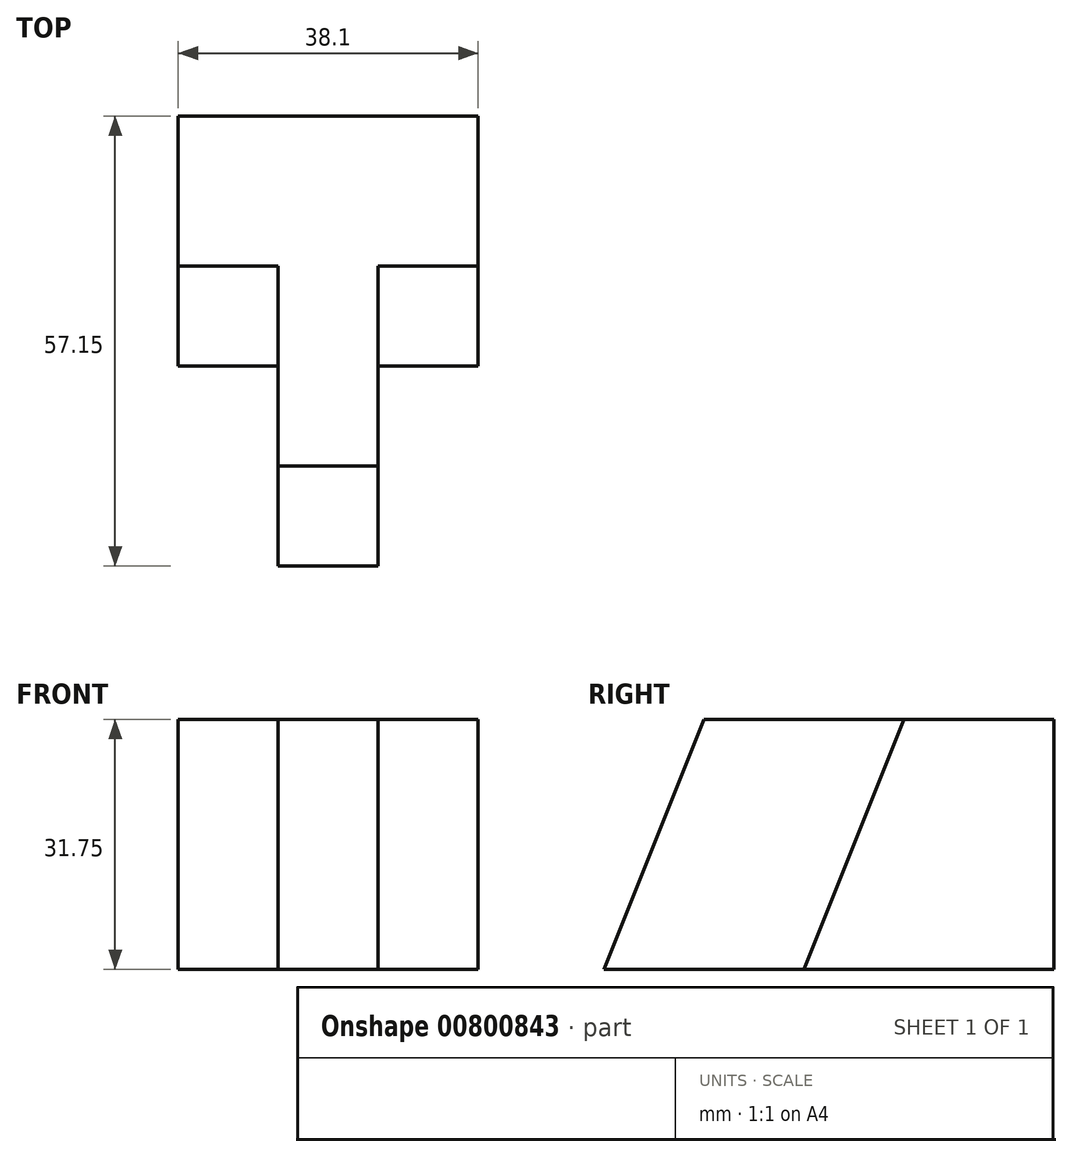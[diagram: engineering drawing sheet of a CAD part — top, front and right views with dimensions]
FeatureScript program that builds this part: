
annotation { "Feature Type Name" : "Feature", "Feature Type Description" : "" }
export const myFeature = defineFeature(function(context is Context, id is Id, definition is map)
    precondition{}
    {
        {
            var Q0;
            Q0=qCreatedBy(makeId("Top.planeOp"),FACE);
            var sketch = newSketch(context, id + "F0", { "sketchPlane" : qUnion([Q0])});
            skLineSegment(sketch, "E0", {"start": v(0, 0) * mm, "end": v(0, 57.15) * mm, "construction": true});
            skLineSegment(sketch, "E1", {"start": v(0, 57.15) * mm, "end": v(38.1, 57.15) * mm});
            skLineSegment(sketch, "E2", {"start": v(0, 57.15) * mm, "end": v(0, 25.4) * mm});
            skLineSegment(sketch, "E3", {"start": v(0, 25.4) * mm, "end": v(12.7, 25.4) * mm});
            skLineSegment(sketch, "E4", {"start": v(12.7, 25.4) * mm, "end": v(12.7, 0) * mm});
            skLineSegment(sketch, "E5", {"start": v(38.1, 57.15) * mm, "end": v(38.1, 25.4) * mm});
            skLineSegment(sketch, "E6", {"start": v(38.1, 25.4) * mm, "end": v(25.4, 25.4) * mm});
            skLineSegment(sketch, "E7", {"start": v(25.4, 25.4) * mm, "end": v(25.4, 0) * mm});
            skLineSegment(sketch, "E8", {"start": v(25.4, 0) * mm, "end": v(12.7, 0) * mm});
            skSolve(sketch);
        }
        {
            var Q0;
            Q0=makeQuery(id+"F0.imprint","IMPRINT",FACE,{"disambiguationData":[TD([[makeQuery(id+"F0.imprint","IMPRINT",EDGE,{"derivedFrom":sQuery(id+"F0.wireOp",EDGE,"E1")}),-1.0]])]});
            extrude(context, id + "F1", {"entities" : qUnion([Q0]), "depth" : 31.75 * mm, "offsetDistance" : 25.4 * mm});
        }
        {
            var Q0;
            Q0=makeQuery(id+"F1.opExtrude","SWEPT_FACE",FACE,{"disambiguationData":[OSD([sQuery(id+"F0.wireOp",EDGE,"E2")])]});
            var sketch = newSketch(context, id + "F2", { "sketchPlane" : qUnion([Q0])});
            skLineSegment(sketch, "E9", {"start": v(-25.4, 31.75) * mm, "end": v(-38.1, 31.75) * mm});
            skLineSegment(sketch, "E10", {"start": v(-38.1, 31.75) * mm, "end": v(-25.4, 0) * mm});
            skSolve(sketch);
        }
        {
            var Q0;
            Q0=makeQuery(id+"F2.imprint","IMPRINT",FACE,{"disambiguationData":[TD([[makeQuery(id+"F2.imprint","IMPRINT",EDGE,{"derivedFrom":sQuery(id+"F2.wireOp",EDGE,"E9")}),-1.0]])]});
            extrude(context, id + "F3", {"entities" : qUnion([Q0]), "operationType" : NewBodyOperationType.REMOVE, "oppositeDirection" : true, "depth" : 12.7 * mm, "offsetDistance" : 25.4 * mm});
        }
        {
            var Q0;
            Q0=makeQuery(id+"F3.boolean.opBoolean","MERGE",FACE,{"derivedFrom":[makeQuery(id+"F1.opExtrude","SWEPT_FACE",FACE,{"disambiguationData":[OSD([sQuery(id+"F0.wireOp",EDGE,"E4")])]}),makeQuery(id+"F3.opExtrude","CAP_FACE",FACE,{"disambiguationData":[OSD([sQuery(id+"F0.wireOp",EDGE,"E2"),sQuery(id+"F0.wireOp",EDGE,"E3"),sQuery(id+"F2.wireOp",EDGE,"E9"),sQuery(id+"F2.wireOp",EDGE,"E10")])],"isStart":false})]});
            var sketch = newSketch(context, id + "F4", { "sketchPlane" : qUnion([Q0])});
            skLineSegment(sketch, "E11", {"start": v(0, 31.75) * mm, "end": v(-12.7, 31.75) * mm});
            skLineSegment(sketch, "E12", {"start": v(-12.7, 31.75) * mm, "end": v(0, 0) * mm});
            skSolve(sketch);
        }
        {
            var Q0;
            Q0=makeQuery(id+"F4.imprint","IMPRINT",FACE,{"disambiguationData":[TD([[makeQuery(id+"F4.imprint","IMPRINT",EDGE,{"derivedFrom":sQuery(id+"F4.wireOp",EDGE,"E11")}),-1.0]])]});
            extrude(context, id + "F5", {"entities" : qUnion([Q0]), "operationType" : NewBodyOperationType.REMOVE, "oppositeDirection" : true, "depth" : 12.7 * mm, "offsetDistance" : 25.4 * mm});
        }
        {
            var Q0;
            Q0=makeQuery(id+"F1.opExtrude","SWEPT_FACE",FACE,{"disambiguationData":[OSD([sQuery(id+"F0.wireOp",EDGE,"E5")])]});
            var sketch = newSketch(context, id + "F6", { "sketchPlane" : qUnion([Q0])});
            skLineSegment(sketch, "E13", {"start": v(25.4, 31.75) * mm, "end": v(38.1, 31.75) * mm});
            skLineSegment(sketch, "E14", {"start": v(38.1, 31.75) * mm, "end": v(25.4, 0) * mm});
            skSolve(sketch);
        }
        {
            var Q0;
            Q0=makeQuery(id+"F6.imprint","IMPRINT",FACE,{"disambiguationData":[TD([[makeQuery(id+"F6.imprint","IMPRINT",EDGE,{"derivedFrom":sQuery(id+"F6.wireOp",EDGE,"E13")}),1.0]])]});
            extrude(context, id + "F7", {"entities" : qUnion([Q0]), "operationType" : NewBodyOperationType.REMOVE, "oppositeDirection" : true, "depth" : 12.7 * mm, "offsetDistance" : 25.4 * mm});
        }
    });
